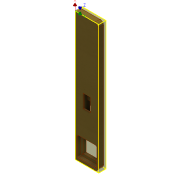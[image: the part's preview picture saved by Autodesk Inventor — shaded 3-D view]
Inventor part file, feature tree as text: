
AUTODESK INVENTOR PART (.ipt)
format: ipt  version: 2018 (Build 220112000, 112)  size: 650,240 bytes
history: native  units: mm
features: sketch x12, extrude x9, fillet x6, projected_geometry x2, plane x1
ambient origin geometry x8: Origin, YZ Plane, XZ Plane, XY Plane, X Axis, Y Axis, Z Axis, Center Point
bodies: Body1 (feature_tree)
feature tree (30):
  extrude  "Extrusion1"  Depth=500.0mm
  extrude  "Extrusion6"  Depth=25.1mm
  sketch  "Sketch7"  dims[d37=88.1mm d38=32.45mm]
  plane  "Work Plane2"
  extrude  "Extrusion9"  Depth=32.45mm
  extrude  "Extrusion11"  Depth=20.0mm TaperAngle=0.0deg
  extrude  "Extrusion12"  Depth=2.0mm
  sketch  "Sketch14"  dims[d68=10.0mm d69=2.5mm]
  fillet  "Fillet14"  Radius=19.0mm
  fillet  "Fillet15"  Radius=2.0mm
  extrude  "Extrusion14"  Depth=55.0mm
  fillet  "Fillet16"  Radius=55.0mm
  fillet  "Fillet17"  Radius=17.5mm
  fillet  "Fillet18"  Radius=30.0mm
  fillet  "Fillet19"  Radius=14.0mm
  extrude  "Extrusion18"  Depth=10.0mm
  sketch  "Sketch23"  dims[d76=5.0mm]
  extrude  "Extrusion19"  Depth=4.1mm
  extrude  "Extrusion20"  Depth=4.1mm
  sketch  "Sketch1"  dims[d0=90.0mm d1=500.0mm]
  sketch  "Sketch6"  dims[d4=25.0mm d5=0.0mm d36=25.1mm]
  projected_geometry  "Projected Loop1"
  sketch  "Sketch9"  dims[d39=100.0mm d40=20.0mm d41=0.0mm]
  sketch  "Sketch12"  dims[d42=16.0mm d43=19.0mm d44=19.0mm d49=2.0mm]
  sketch  "Sketch13"  dims[d50=22.0mm d51=0.0mm d57=55.0mm d58=55.0mm d59=17.5mm d61=30.0mm d62=0.0mm d64=14.0mm d65=0.0mm]
  sketch  "Sketch15"  dims[d70=4.1mm d71=4.1mm]
  sketch  "Sketch22"  dims[d72=4.1mm d73=4.1mm]
  projected_geometry  "Projected Loop5"
  sketch  "Sketch24"  dims[d77=2.0mm]
  sketch  "Sketch25"  dims[d81=25.1mm d82=50.0mm d83=32.45mm d84=188.375mm d85=15.0mm d86=0.0mm d87=2.0mm d88=2.0mm d97=3.0mm d98=5.0mm d99=15.0mm d100=20.0mm d101=6.0mm d102=0.0mm d103=1.0mm d104=0.0mm d105=1.0mm d106=0.0mm]
